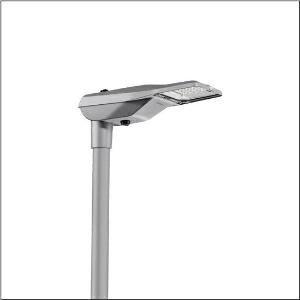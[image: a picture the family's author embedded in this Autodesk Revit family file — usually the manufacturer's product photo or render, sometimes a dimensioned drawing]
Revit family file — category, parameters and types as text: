
# Revit family: streetlight_sl_21_iq_micro___p0_8a_5xe1u31y08db_9c46
name_source: partatom
category: Lighting Fixtures
units: mm (PartAtom-declared; Revit-internal decimal feet)

## family parameters
Cut with Voids When Loaded = No
Host = Face
Light Source = No
Part Type = Normal
Room Calculation Point = No
Round Connector Dimension = Use Diameter
Shared = No

## types (1)
- --- (1 x LED, 5130 lm, 39.1 W, 3000K)
    Apparent Load = 39 VA
    CIE Flux Codes = 33 69 96 100 100
    Color Rendering = 70
    Color Temperature = 3000K
    Default Elevation = 1800 mm
    Description = Streetlight SL 21 iQ micro, mast luminaire, primary light control with lens, of PMMA, primary optical cover: cover, of toughened safety glass, transparent, light distribution: P0.8a, light emission: direct distribution, primary light characteristic: asymmetric, installation type: post-top, side-entry, LED, High Power LED, rated luminous flux: 5.130lm, luminous efficacy: 131lm/W, light colour: 730, colour temperature: 3000K, control gear: iQ-Street Remote, D4i with power reduction, control: pre-setting: logarithmic dimming characteristic, Street-Remote, Auto-Match, Temp-Guard, Lumen-Switch, Night-Set, Smart-Wire, Light-Fading, Desk-Remote (wireless, voltage-free reading and setting of iQ features in the workshop via application-optimized NFC function/RFID function), optimised constant luminous flux control (CLO 2.0), mains connection: 220..240V, AC, 50/60Hz, start of lifetime: 39W, end of service life: 41W, reduction: 17W, luminaire housing, of diecast aluminium, powder-coated, SITECO metallic grey (DB 702S), corrosivity category C5 high according to DIN EN ISO 12944, please order mast flange separately, inclination adjustable: 0°, 5°, 10°, 15°, sealing non-destructively replaceable, multi-level sealing system, length: 528mm, width: 235mm, height: 110mm, mast flange for spigot size: 42mm (side-entry): 5XC10008XM4, 60/48mm (side-entry/post-top): 5XC10108XM2, 76/60mm (side-entry/post-top): 5XC10108XM1, mounting height: 4..8m, Smart Interface below and above, protection rating (complete): IP66, insulation class (complete): insulation class II (safety insulation), certification: CE, ENEC, ENEC+, VDE, impact resistance: IK10, permissible operating ambient temperature for outdoor applications: -40..+50°C, standard-compliant lighting for roads and squares, packaging unit: 1 piece

Light Distribution: P0.8a
    Height = 110 mm
    Lamp = 1 x LED
    Lamp Light Flux = 5130 lm
    Lamp Power = 39.1 W
    Lamp count = 1
    Length = 528 mm
    Luminous efficacy = 131 lm/W
    Manufacturer = Siteco
    ModVariant = No
    Model = 5XE1U31Y08DB
    Mounting Place = Pole
    Mounting Type = Pole top
    Number of Poles = 1
    OnlyDefault = Yes
    Power Factor = 1
    Product Name = Streetlight SL 21 iQ micro | P0.8a
    Product group = mast luminaire | pylon top
    ProductGroupID = 6100
    Protection Class = Protection class II
    Protection Degree = IP 66
    RLX_Detail_Level = 1
    RLX_Emergency_Light_Flux = 0 lm
    RLX_Emergency_Type = 0
    RLX_Emergency_Type_DB = No
    RlxData = <blob elided: 99045 chars, md5=f8e9f5dc>
    Socket = socket
    Standby Power = 0 W
    System Light Flux = 5130 lm
    System Power = 39 W
    Type Comments = factory setting: luminous flux: 100 % | dim-lin: 254 | 765 mA
    Type Image = l_1007239.jpg
    URL = http://relux.com
    VarID = @adj_083559
    Voltage = 0 V
    Weight = 0.00 kg
    Width = 235 mm

## geometry (parser evidence)
native form markers: Blend x4, Sweep x12
no freeform markers — native parametric forms only
